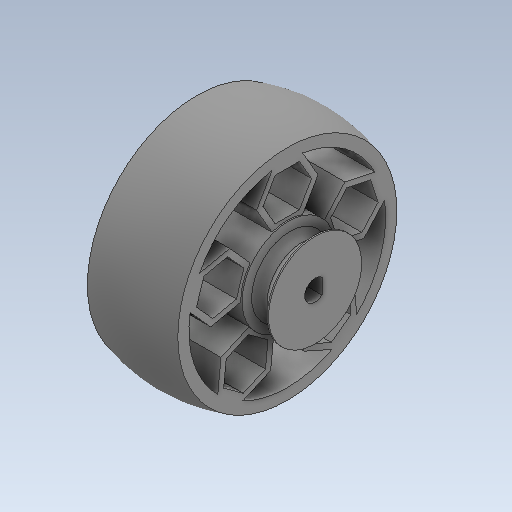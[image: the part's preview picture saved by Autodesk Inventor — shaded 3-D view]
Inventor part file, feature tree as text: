
AUTODESK INVENTOR PART (.ipt)
format: ipt  version: 2020 (Build 240168000, 168)  size: 411,136 bytes
history: native  units: in
note: dims shown in document units (in); Inventor stores cm internally (conversion verified against a paired STEP export)
features: sketch x4, extrude x2, revolve x2, projected_geometry x1
ambient origin geometry x8: Origin, YZ Plane, XZ Plane, XY Plane, X Axis, Y Axis, Z Axis, Center Point
bodies: Solid1 (feature_tree)
feature tree (9):
  extrude  "Extrusion1"  Depth=0.0394in
  sketch  "Sketch3"  dims[d6=0.5276in d7=0.1575in]
  revolve  "Revolution1"  [1 undecoded]
  extrude  "Extrusion2"  Depth=0.1575in
  revolve  "Revolution2"  [1 undecoded]
  sketch  "Sketch1"  dims[d0=0.1181in d1=0.0394in]
  sketch  "Sketch2"  dims[d3=1.2402in d4=0.1181in]
  projected_geometry  "Projected Loop1"
  sketch  "Sketch4"  dims[d8=0.0in d9=1.2402in d10=0.063in d11=0.0315in d16=0.5118in d17=0.0in d19=360.0deg d20=0.0787in d24=0.0394in d25=90.0deg d26=45.0deg d28=0.0079in d29=1.9685in d31=360.0deg]
note: 2 required parameter values undecoded (feature->parameter linkage not recoverable at this tier; creation-order binding heuristic only, values carry confidence <= 0.55)
